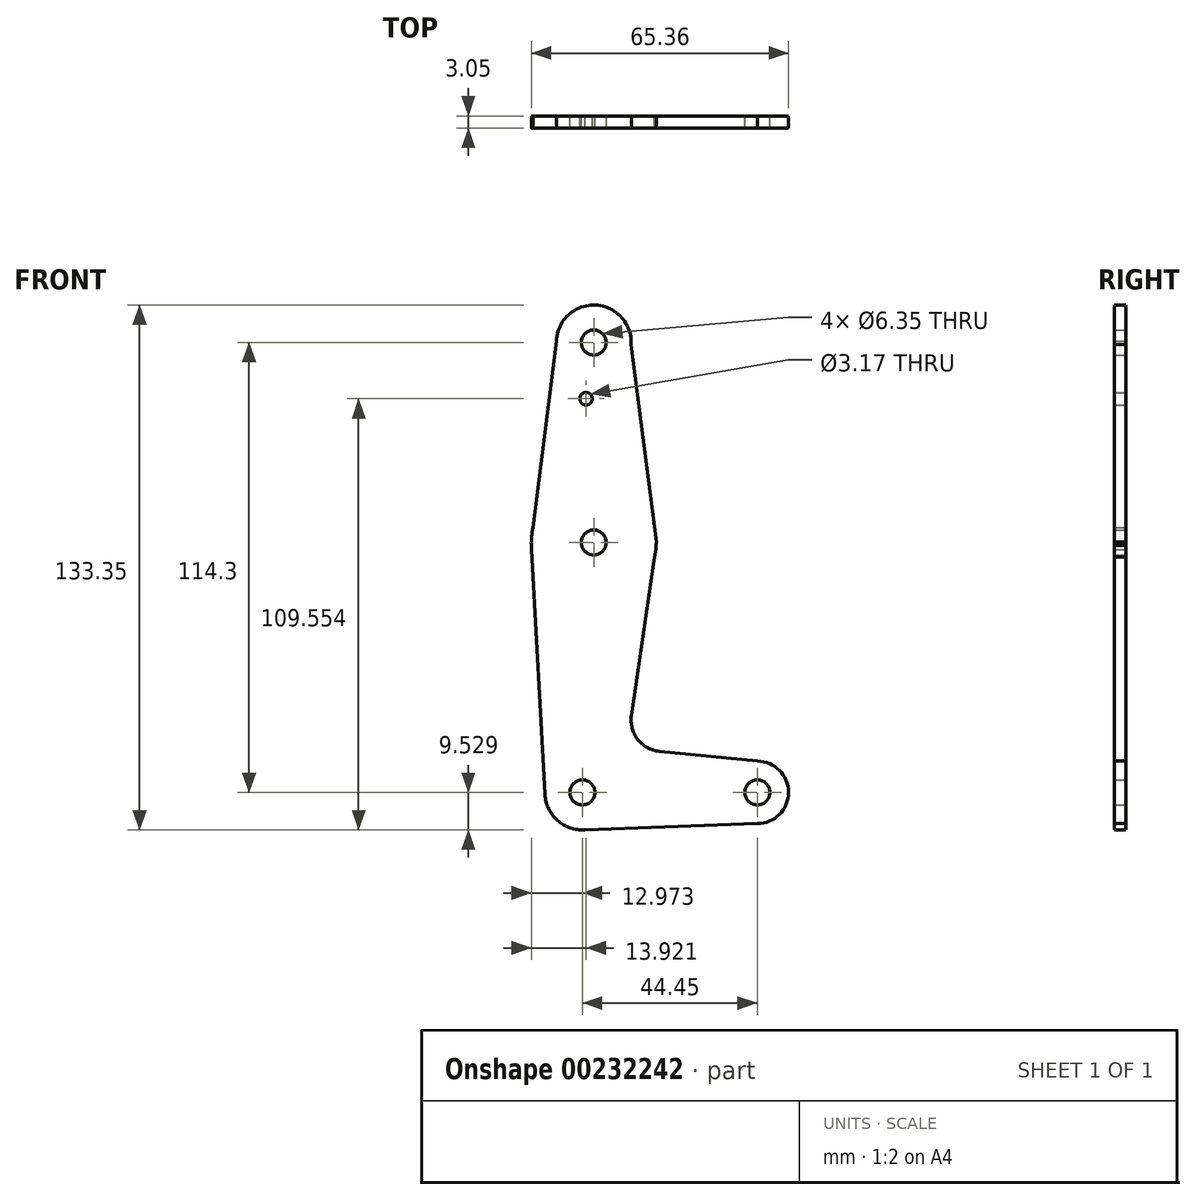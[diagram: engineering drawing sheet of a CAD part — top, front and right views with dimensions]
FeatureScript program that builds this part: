
annotation { "Feature Type Name" : "Feature", "Feature Type Description" : "" }
export const myFeature = defineFeature(function(context is Context, id is Id, definition is map)
    precondition{}
    {
        {
            var Q0;
            Q0=qCreatedBy(makeId("Front.planeOp"),FACE);
            var sketch = newSketch(context, id + "F0", { "sketchPlane" : qUnion([Q0])});
            skLineSegment(sketch, "E0", {"start": v(-21.5, -18.02) * mm, "end": v(22.94, -18.02) * mm, "construction": true});
            skCircle(sketch, "E1", {"center": v(-18.6, 96.28) * mm, "radius": 9.53 * mm});
            skCircle(sketch, "E2", {"center": v(-18.6, 45.48) * mm, "radius": 15.88 * mm});
            skCircle(sketch, "E3", {"center": v(-21.5, -18.02) * mm, "radius": 9.53 * mm});
            skCircle(sketch, "E4", {"center": v(22.94, -18.02) * mm, "radius": 7.94 * mm});
            skLineSegment(sketch, "E5", {"start": v(-18.6, 96.28) * mm, "end": v(-21.5, -18.02) * mm, "construction": true});
            skLineSegment(sketch, "E6", {"start": v(-28.12, 96.69) * mm, "end": v(-34.48, 45.6) * mm});
            skLineSegment(sketch, "E7", {"start": v(-9.1, 95.77) * mm, "end": v(-2.62, 45.6) * mm});
            skLineSegment(sketch, "E8", {"start": v(-34.48, 45.6) * mm, "end": v(-31.02, -18.53) * mm});
            skLineSegment(sketch, "E9", {"start": v(-2.62, 45.6) * mm, "end": v(-9.04, 1.48) * mm});
            skLineSegment(sketch, "E10", {"start": v(-1.97, -7.57) * mm, "end": v(22.94, -10.08) * mm});
            skLineSegment(sketch, "E11", {"start": v(-21.44, -27.55) * mm, "end": v(22.94, -25.96) * mm});
            skCircle(sketch, "E12", {"center": v(-20.56, 82) * mm, "radius": 1.59 * mm});
            skArc(sketch, "E13.filletArc", {"start": v(-9.04, 1.48) * mm, "mid": v(-7.44, -4.55) * mm, "end": v(-1.97, -7.57) * mm});
            skCircle(sketch, "E14", {"center": v(-18.6, 96.28) * mm, "radius": 3.18 * mm});
            skCircle(sketch, "E15", {"center": v(-18.6, 45.48) * mm, "radius": 3.18 * mm});
            skCircle(sketch, "E16", {"center": v(-21.5, -18.02) * mm, "radius": 3.18 * mm});
            skCircle(sketch, "E17", {"center": v(22.94, -18.02) * mm, "radius": 3.18 * mm});
            skSolve(sketch);
        }
        {
            var Q0;
            Q0 = qSketchRegion(id + "F0", true);
            extrude(context, id + "F1", {"entities" : qUnion([Q0]), "depth" : 3.05 * mm});
        }
    });
